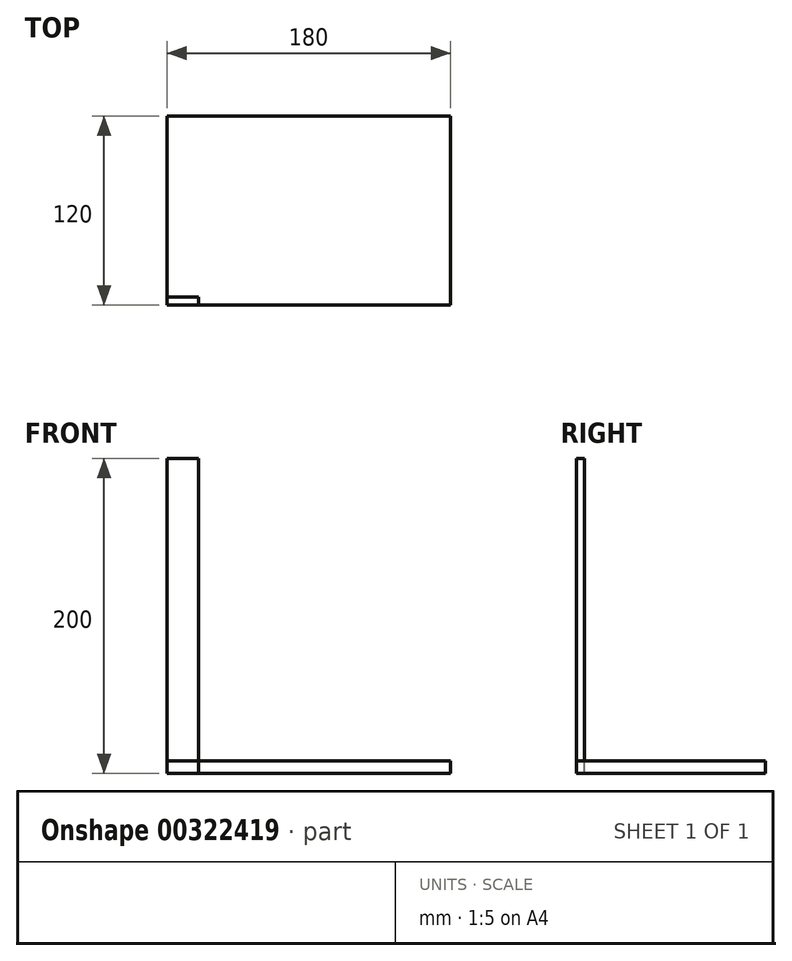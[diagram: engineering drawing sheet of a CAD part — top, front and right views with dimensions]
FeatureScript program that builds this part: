
annotation { "Feature Type Name" : "Feature", "Feature Type Description" : "" }
export const myFeature = defineFeature(function(context is Context, id is Id, definition is map)
    precondition{}
    {
        {
            var Q0;
            Q0=qCreatedBy(makeId("Top.planeOp"),FACE);
            var sketch = newSketch(context, id + "F0", { "sketchPlane" : qUnion([Q0])});
            skLineSegment(sketch, "E0.bottom", {"start": v(0, 0) * mm, "end": v(180, 0) * mm});
            skLineSegment(sketch, "E0.top", {"start": v(0, 120) * mm, "end": v(180, 120) * mm});
            skLineSegment(sketch, "E0.left", {"start": v(0, 0) * mm, "end": v(0, 120) * mm});
            skLineSegment(sketch, "E0.right", {"start": v(180, 0) * mm, "end": v(180, 120) * mm});
            skSolve(sketch);
        }
        {
            var Q0;
            Q0=makeQuery(id+"F0.imprint","IMPRINT",FACE,{"disambiguationData":[TD([[makeQuery(id+"F0.imprint","IMPRINT",EDGE,{"derivedFrom":sQuery(id+"F0.wireOp",EDGE,"E0.bottom")}),1.0]])]});
            extrude(context, id + "F1", {"entities" : qUnion([Q0]), "depth" : 8 * mm});
        }
        {
            var Q0;
            Q0=qCreatedBy(makeId("Front.planeOp"),FACE);
            var sketch = newSketch(context, id + "F2", { "sketchPlane" : qUnion([Q0])});
            skLineSegment(sketch, "E1.bottom", {"start": v(0, 0) * mm, "end": v(20, 0) * mm});
            skLineSegment(sketch, "E1.top", {"start": v(0, 200) * mm, "end": v(20, 200) * mm});
            skLineSegment(sketch, "E1.left", {"start": v(0, 0) * mm, "end": v(0, 200) * mm});
            skLineSegment(sketch, "E1.right", {"start": v(20, 0) * mm, "end": v(20, 200) * mm});
            skSolve(sketch);
        }
        {
            var Q0;
            Q0 = qSketchRegion(id + "F2", true);
            extrude(context, id + "F3", {"entities" : qUnion([Q0]), "oppositeDirection" : true, "depth" : 5 * mm});
        }
    });
